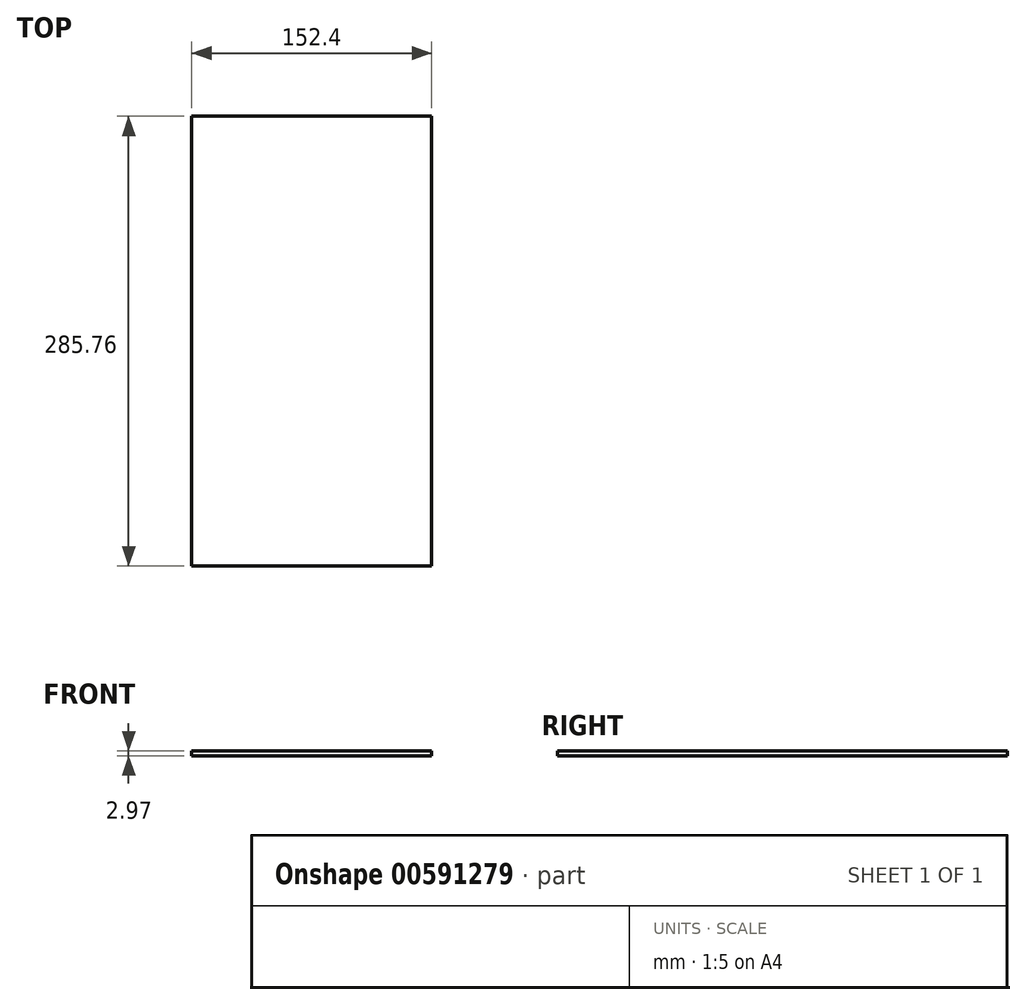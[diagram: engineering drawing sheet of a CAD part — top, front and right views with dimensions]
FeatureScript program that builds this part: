
annotation { "Feature Type Name" : "Feature", "Feature Type Description" : "" }
export const myFeature = defineFeature(function(context is Context, id is Id, definition is map)
    precondition{}
    {
        {
            var Q0;
            Q0=qCreatedBy(makeId("Top.planeOp"),FACE);
            var sketch = newSketch(context, id + "F0", { "sketchPlane" : qUnion([Q0])});
            skLineSegment(sketch, "E0.bottom", {"start": v(76.2, -142.88) * mm, "end": v(-76.2, -142.88) * mm});
            skLineSegment(sketch, "E0.top", {"start": v(76.2, 142.88) * mm, "end": v(-76.2, 142.88) * mm});
            skLineSegment(sketch, "E0.left", {"start": v(76.2, -142.88) * mm, "end": v(76.2, 142.88) * mm});
            skLineSegment(sketch, "E0.right", {"start": v(-76.2, -142.88) * mm, "end": v(-76.2, 142.88) * mm});
            skPoint(sketch, "E0.middle", {"position": v(0, 0) * mm});
            skSolve(sketch);
        }
        {
            var Q0;
            Q0=makeQuery(id+"F0.imprint","IMPRINT",FACE,{"disambiguationData":[TD([[makeQuery(id+"F0.imprint","IMPRINT",EDGE,{"derivedFrom":sQuery(id+"F0.wireOp",EDGE,"E0.bottom")}),-1.0]])]});
            extrude(context, id + "F1", {"entities" : qUnion([Q0]), "depth" : 2.97 * mm, "offsetDistance" : 25.4 * mm});
        }
    });
